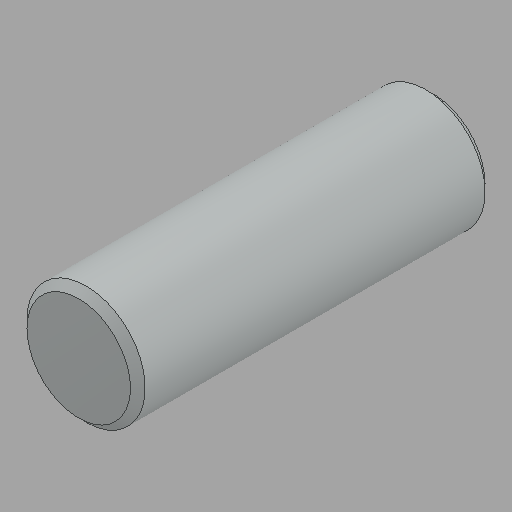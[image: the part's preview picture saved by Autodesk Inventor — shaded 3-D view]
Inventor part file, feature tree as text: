
AUTODESK INVENTOR PART (.ipt)
format: ipt  version: 2024.2 (Build 282272000, 272)  size: 102,400 bytes
history: native  units: in
note: dims shown in document units (in); Inventor stores cm internally (conversion verified against a paired STEP export)
features: chamfer x1
ambient origin geometry x8: Origin, YZ Plane, XZ Plane, XY Plane, X Axis, Y Axis, Z Axis, Center Point
bodies: Solid1 (feature_tree)
feature tree (1):
  chamfer  "Chamfer1"  [1 undecoded]
note: 1 required parameter value undecoded (feature->parameter linkage not recoverable at this tier; creation-order binding heuristic only, values carry confidence <= 0.55)
